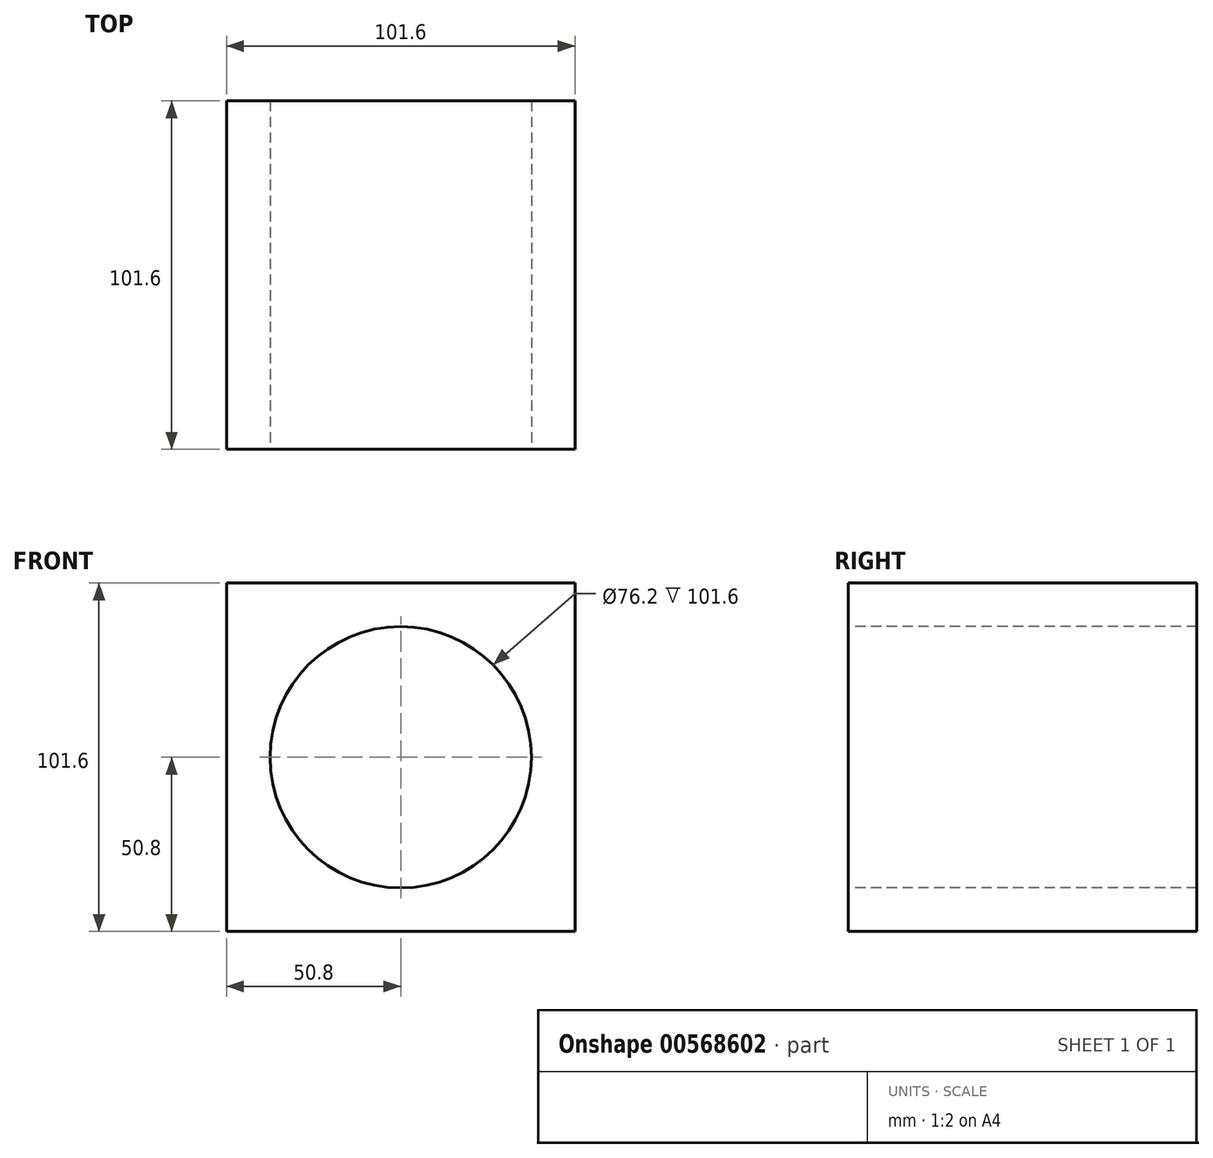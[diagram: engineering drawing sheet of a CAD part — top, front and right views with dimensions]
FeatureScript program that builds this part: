
annotation { "Feature Type Name" : "Feature", "Feature Type Description" : "" }
export const myFeature = defineFeature(function(context is Context, id is Id, definition is map)
    precondition{}
    {
        {
            var Q0;
            Q0=qCreatedBy(makeId("Top.planeOp"),FACE);
            var sketch = newSketch(context, id + "F0", { "sketchPlane" : qUnion([Q0])});
            skLineSegment(sketch, "E0.bottom", {"start": v(0, 0) * mm, "end": v(101.6, 0) * mm});
            skLineSegment(sketch, "E0.top", {"start": v(0, 101.6) * mm, "end": v(101.6, 101.6) * mm});
            skLineSegment(sketch, "E0.left", {"start": v(0, 0) * mm, "end": v(0, 101.6) * mm});
            skLineSegment(sketch, "E0.right", {"start": v(101.6, 0) * mm, "end": v(101.6, 101.6) * mm});
            skSolve(sketch);
        }
        {
            var Q0;
            Q0=makeQuery(id+"F0.imprint","IMPRINT",FACE,{"disambiguationData":[TD([[makeQuery(id+"F0.imprint","IMPRINT",EDGE,{"derivedFrom":sQuery(id+"F0.wireOp",EDGE,"E0.bottom")}),1.0]])]});
            extrude(context, id + "F1", {"entities" : qUnion([Q0]), "depth" : 101.6 * mm, "offsetDistance" : 25.4 * mm});
        }
        {
            var Q0;
            Q0=makeQuery(id+"F1.opExtrude","SWEPT_FACE",FACE,{"disambiguationData":[OSD([sQuery(id+"F0.wireOp",EDGE,"E0.bottom")])]});
            var sketch = newSketch(context, id + "F2", { "sketchPlane" : qUnion([Q0])});
            skCircle(sketch, "E1", {"center": v(50.8, 50.8) * mm, "radius": 38.1 * mm});
            skPoint(sketch, "E1.centerSnap0", {"position": v(50.8, 0) * mm});
            skPoint(sketch, "E1.centerSnap1", {"position": v(0, 50.8) * mm});
            skSolve(sketch);
        }
        {
            var Q0;
            Q0=makeQuery(id+"F2.imprint","IMPRINT",FACE,{"disambiguationData":[TD([[makeQuery(id+"F2.imprint","IMPRINT",EDGE,{"derivedFrom":sQuery(id+"F2.wireOp",EDGE,"E1")}),1.0]])]});
            extrude(context, id + "F3", {"entities" : qUnion([Q0]), "operationType" : NewBodyOperationType.REMOVE, "endBound" : BoundingType.THROUGH_ALL, "oppositeDirection" : true, "depth" : 25.4 * mm, "offsetDistance" : 25.4 * mm});
        }
    });
